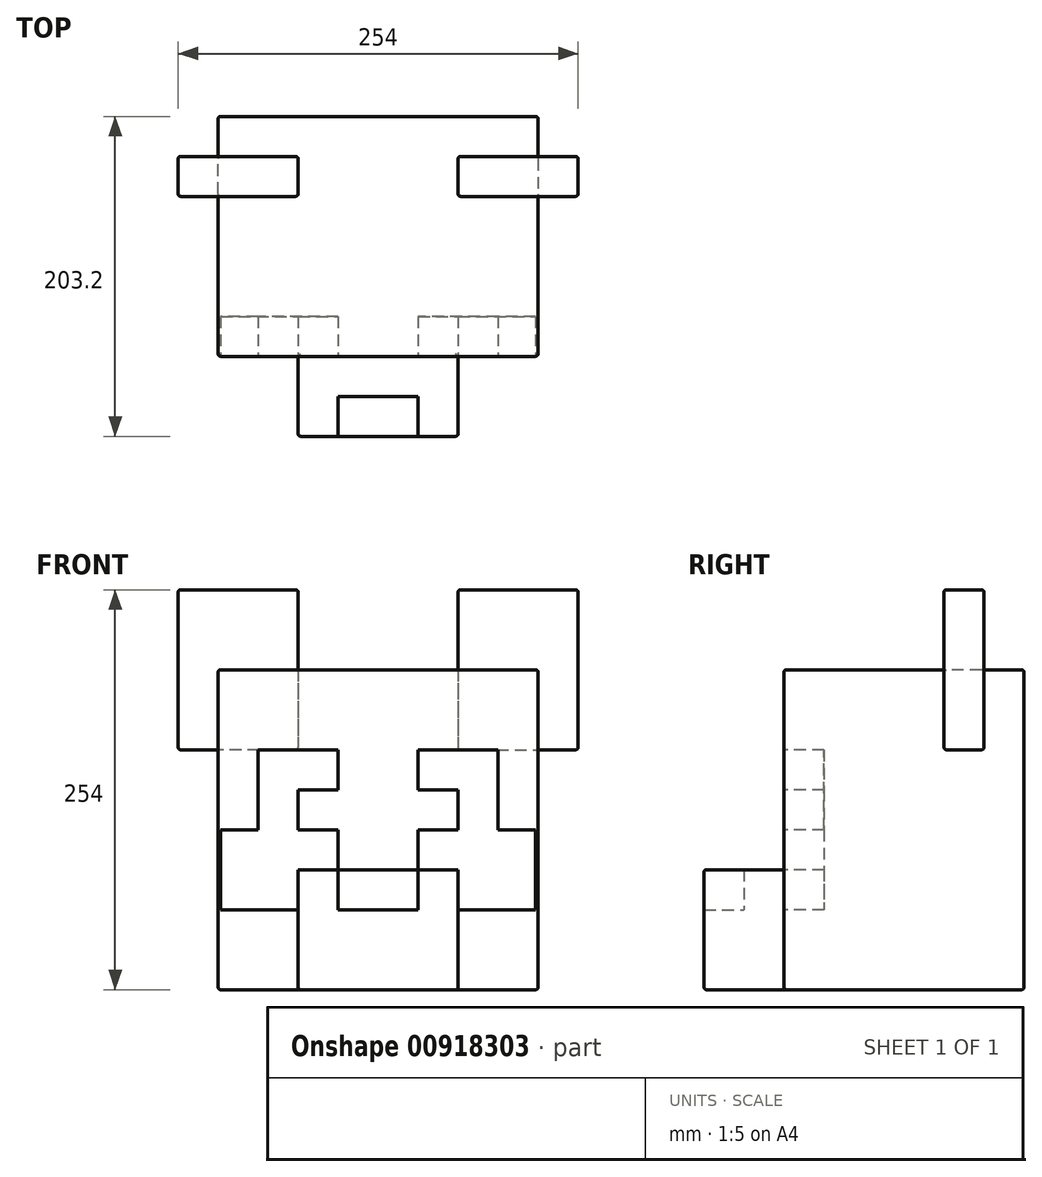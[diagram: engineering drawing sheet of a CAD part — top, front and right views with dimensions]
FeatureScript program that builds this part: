
annotation { "Feature Type Name" : "Feature", "Feature Type Description" : "" }
export const myFeature = defineFeature(function(context is Context, id is Id, definition is map)
    precondition{}
    {
        {
            var Q0;
            Q0=qCreatedBy(makeId("Front.planeOp"),FACE);
            var sketch = newSketch(context, id + "F0", { "sketchPlane" : qUnion([Q0])});
            skLineSegment(sketch, "E0", {"start": v(25.4, 50.8) * mm, "end": v(25.4, 25.4) * mm});
            skLineSegment(sketch, "E1", {"start": v(25.4, 25.4) * mm, "end": v(50.8, 25.4) * mm});
            skLineSegment(sketch, "E2", {"start": v(50.8, 25.4) * mm, "end": v(50.8, 0) * mm});
            skLineSegment(sketch, "E3.bottom", {"start": v(101.6, 101.6) * mm, "end": v(-101.6, 101.6) * mm});
            skLineSegment(sketch, "E3.top", {"start": v(101.6, -101.6) * mm, "end": v(-101.6, -101.6) * mm});
            skLineSegment(sketch, "E3.left", {"start": v(101.6, 101.6) * mm, "end": v(101.6, -101.6) * mm});
            skLineSegment(sketch, "E3.right", {"start": v(-101.6, 101.6) * mm, "end": v(-101.6, -101.6) * mm});
            skPoint(sketch, "E3.middle", {"position": v(0, 0) * mm});
            skPoint(sketch, "E4", {"position": v(101.6, 76.2) * mm});
            skPoint(sketch, "E5", {"position": v(101.6, 50.8) * mm});
            skPoint(sketch, "E6", {"position": v(101.6, 25.4) * mm});
            skPoint(sketch, "E7", {"position": v(101.6, 0) * mm});
            skPoint(sketch, "E8", {"position": v(101.6, -25.4) * mm});
            skPoint(sketch, "E9", {"position": v(101.6, -50.8) * mm});
            skPoint(sketch, "E10", {"position": v(101.6, -76.2) * mm});
            skPoint(sketch, "E11", {"position": v(76.2, 101.6) * mm});
            skPoint(sketch, "E12", {"position": v(50.8, 101.6) * mm});
            skPoint(sketch, "E13", {"position": v(25.4, 101.6) * mm});
            skPoint(sketch, "E14", {"position": v(0, 101.6) * mm});
            skPoint(sketch, "E15", {"position": v(-25.4, 101.6) * mm});
            skPoint(sketch, "E16", {"position": v(-50.8, 101.6) * mm});
            skPoint(sketch, "E17", {"position": v(-76.2, 101.6) * mm});
            skLineSegment(sketch, "E18", {"start": v(25.4, 50.8) * mm, "end": v(76.2, 50.8) * mm});
            skLineSegment(sketch, "E19", {"start": v(50.8, 0) * mm, "end": v(25.4, 0) * mm});
            skLineSegment(sketch, "E20", {"start": v(25.4, 0) * mm, "end": v(25.4, -25.4) * mm});
            skLineSegment(sketch, "E21", {"start": v(25.4, -25.4) * mm, "end": v(50.8, -25.4) * mm});
            skLineSegment(sketch, "E22", {"start": v(50.8, -25.4) * mm, "end": v(50.8, -50.8) * mm});
            skLineSegment(sketch, "E23", {"start": v(50.8, -50.8) * mm, "end": v(101.6, -50.8) * mm});
            skLineSegment(sketch, "E24", {"start": v(76.2, 50.8) * mm, "end": v(76.2, 0) * mm});
            skLineSegment(sketch, "E25", {"start": v(50.8, -50.8) * mm, "end": v(50.8, -101.6) * mm});
            skLineSegment(sketch, "E26", {"start": v(0, 101.6) * mm, "end": v(0, -101.6) * mm, "construction": true});
            skLineSegment(sketch, "E27.MirrorCS", {"start": v(-50.8, -25.4) * mm, "end": v(-50.8, -50.8) * mm});
            skLineSegment(sketch, "E28.MirrorCS", {"start": v(-25.4, 50.8) * mm, "end": v(-76.2, 50.8) * mm});
            skLineSegment(sketch, "E29.MirrorCS", {"start": v(-50.8, -50.8) * mm, "end": v(-101.6, -50.8) * mm});
            skLineSegment(sketch, "E30.MirrorCS", {"start": v(-25.4, 0) * mm, "end": v(-25.4, -25.4) * mm});
            skLineSegment(sketch, "E31.MirrorCS", {"start": v(-76.2, 50.8) * mm, "end": v(-76.2, 0) * mm});
            skLineSegment(sketch, "E32.MirrorCS", {"start": v(-25.4, -25.4) * mm, "end": v(-50.8, -25.4) * mm});
            skLineSegment(sketch, "E33.MirrorCS", {"start": v(-25.4, 25.4) * mm, "end": v(-50.8, 25.4) * mm});
            skLineSegment(sketch, "E34.MirrorCS", {"start": v(-50.8, 0) * mm, "end": v(-25.4, 0) * mm});
            skLineSegment(sketch, "E35.MirrorCS", {"start": v(-50.8, -50.8) * mm, "end": v(-50.8, -101.6) * mm});
            skLineSegment(sketch, "E36.MirrorCS", {"start": v(-25.4, 50.8) * mm, "end": v(-25.4, 25.4) * mm});
            skLineSegment(sketch, "E37.MirrorCS", {"start": v(-50.8, 25.4) * mm, "end": v(-50.8, 0) * mm});
            skLineSegment(sketch, "E38", {"start": v(-25.4, -25.4) * mm, "end": v(25.4, -25.4) * mm});
            skPoint(sketch, "E39.MirrorCS.end.orphan", {"position": v(-101.6, 25.4) * mm});
            skLineSegment(sketch, "E40", {"start": v(76.2, 0) * mm, "end": v(101.6, 0) * mm});
            skLineSegment(sketch, "E41.MirrorCS", {"start": v(-76.2, 0) * mm, "end": v(-101.6, 0) * mm});
            skSolve(sketch);
        }
        {
            var Q0;
            Q0=makeQuery(id+"F0.imprint","IMPRINT",FACE,{"disambiguationData":[TD([[makeQuery(id+"F0.imprint","IMPRINT",EDGE,{"derivedFrom":sQuery(id+"F0.wireOp",EDGE,"E0")}),-1.0]])]});
            var Q1;
            Q1=makeQuery(id+"F0.imprint","IMPRINT",FACE,{"disambiguationData":[TD([[makeQuery(id+"F0.imprint","IMPRINT",EDGE,{"derivedFrom":sQuery(id+"F0.wireOp",EDGE,"E28.MirrorCS")}),1.0]])]});
            var Q2;
            Q2=makeQuery(id+"F0.imprint","IMPRINT",FACE,{"disambiguationData":[TD([[makeQuery(id+"F0.imprint","IMPRINT",EDGE,{"derivedFrom":sQuery(id+"F0.wireOp",EDGE,"E0")}),1.0]])]});
            var Q3;
            Q3=makeQuery(id+"F0.imprint","IMPRINT",FACE,{"disambiguationData":[TD([[makeQuery(id+"F0.imprint","IMPRINT",EDGE,{"derivedFrom":sQuery(id+"F0.wireOp",EDGE,"E27.MirrorCS")}),-1.0]])]});
            var Q4;
            Q4=makeQuery(id+"F0.imprint","IMPRINT",FACE,{"disambiguationData":[TD([[makeQuery(id+"F0.imprint","IMPRINT",EDGE,{"derivedFrom":sQuery(id+"F0.wireOp",EDGE,"E2")}),1.0]])]});
            var Q5;
            {var subQ4=sQuery(id+"F0.wireOp",EDGE,"E29.MirrorCS");Q5=makeQuery(id+"F0.imprint","IMPRINT",FACE,{"disambiguationData":[TD([[makeQuery(id+"F0.imprint","IMPRINT",EDGE,{"derivedFrom":subQ4}),1.0]])]});}
            var Q6;
            Q6=makeQuery(id+"F0.imprint","IMPRINT",FACE,{"disambiguationData":[TD([[makeQuery(id+"F0.imprint","IMPRINT",EDGE,{"derivedFrom":sQuery(id+"F0.wireOp",EDGE,"E21")}),-1.0]])]});
            var Q7;
            {var subQ4=sQuery(id+"F0.wireOp",EDGE,"E23");Q7=makeQuery(id+"F0.imprint","IMPRINT",FACE,{"disambiguationData":[TD([[makeQuery(id+"F0.imprint","IMPRINT",EDGE,{"derivedFrom":subQ4}),-1.0]])]});}
            extrude(context, id + "F1", {"entities" : qUnion([Q0, Q1, Q2, Q3, Q4, Q5, Q6, Q7]), "oppositeDirection" : true, "depth" : 152.4 * mm, "offsetDistance" : 25.4 * mm});
        }
        {
            var Q0;
            Q0=makeQuery(id+"F0.imprint","IMPRINT",FACE,{"disambiguationData":[TD([[makeQuery(id+"F0.imprint","IMPRINT",EDGE,{"derivedFrom":sQuery(id+"F0.wireOp",EDGE,"E21")}),-1.0]])]});
            extrude(context, id + "F2", {"entities" : qUnion([Q0]), "operationType" : NewBodyOperationType.ADD, "depth" : 50.8 * mm, "offsetDistance" : 25.4 * mm});
        }
        {
            var Q0;
            Q0=makeQuery(id+"F2.opExtrude","CAP_FACE",FACE,{"disambiguationData":[OSD([sQuery(id+"F0.wireOp",EDGE,"E3.top"),sQuery(id+"F0.wireOp",EDGE,"E21"),sQuery(id+"F0.wireOp",EDGE,"E22"),sQuery(id+"F0.wireOp",EDGE,"E25"),sQuery(id+"F0.wireOp",EDGE,"E27.MirrorCS"),sQuery(id+"F0.wireOp",EDGE,"E32.MirrorCS"),sQuery(id+"F0.wireOp",EDGE,"E35.MirrorCS"),sQuery(id+"F0.wireOp",EDGE,"E38")])],"isStart":false});
            var sketch = newSketch(context, id + "F3", { "sketchPlane" : qUnion([Q0])});
            skLineSegment(sketch, "E42", {"start": v(-25.4, -25.4) * mm, "end": v(25.4, -25.4) * mm});
            skLineSegment(sketch, "E43", {"start": v(25.4, -25.4) * mm, "end": v(25.4, -50.8) * mm});
            skLineSegment(sketch, "E44", {"start": v(25.4, -50.8) * mm, "end": v(-25.4, -50.8) * mm});
            skLineSegment(sketch, "E45", {"start": v(-25.4, -50.8) * mm, "end": v(-25.4, -25.4) * mm});
            skSolve(sketch);
        }
        {
            var Q0;
            Q0=makeQuery(id+"F3.imprint","IMPRINT",FACE,{"disambiguationData":[TD([[makeQuery(id+"F3.imprint","IMPRINT",EDGE,{"derivedFrom":sQuery(id+"F3.wireOp",EDGE,"E42")}),-1.0]])]});
            extrude(context, id + "F4", {"entities" : qUnion([Q0]), "operationType" : NewBodyOperationType.REMOVE, "oppositeDirection" : true, "depth" : 25.4 * mm, "offsetDistance" : 25.4 * mm});
        }
        {
            var Q0;
            Q0=makeQuery(id+"F4.boolean.opBoolean","COPY",FACE,{"derivedFrom":makeQuery(id+"F4.opExtrude","CAP_FACE",FACE,{"disambiguationData":[OSD([sQuery(id+"F3.wireOp",EDGE,"E42"),sQuery(id+"F3.wireOp",EDGE,"E43"),sQuery(id+"F3.wireOp",EDGE,"E44"),sQuery(id+"F3.wireOp",EDGE,"E45")])],"isStart":false})});
            extrude(context, id + "F5", {"entities" : qUnion([Q0]), "depth" : 25.4 * mm, "offsetDistance" : 25.4 * mm});
        }
        {
            var Q0;
            Q0=qCreatedBy(makeId("Front.planeOp"),FACE);
            cPlane(context, id + "F6", {"entities" : qUnion([Q0]), "cplaneType" : CPlaneType.OFFSET, "offset" : 101.6 * mm, "oppositeDirection" : true, "width" : 152.4 * mm, "height" : 152.4 * mm});
        }
        {
            var Q0;
            Q0=qCreatedBy(id+"F6.planeOp",FACE);
            var sketch = newSketch(context, id + "F7", { "sketchPlane" : qUnion([Q0])});
            skLineSegment(sketch, "E46", {"start": v(50.8, 101.6) * mm, "end": v(50.8, 152.4) * mm});
            skLineSegment(sketch, "E47", {"start": v(50.8, 152.4) * mm, "end": v(127, 152.4) * mm});
            skLineSegment(sketch, "E48", {"start": v(127, 152.4) * mm, "end": v(127, 50.8) * mm});
            skLineSegment(sketch, "E49", {"start": v(127, 50.8) * mm, "end": v(101.6, 50.8) * mm});
            skLineSegment(sketch, "E50", {"start": v(101.6, 50.8) * mm, "end": v(101.6, 101.6) * mm});
            skLineSegment(sketch, "E51", {"start": v(101.6, 101.6) * mm, "end": v(50.8, 101.6) * mm});
            skLineSegment(sketch, "E52", {"start": v(50.8, 101.6) * mm, "end": v(50.8, 50.8) * mm});
            skLineSegment(sketch, "E53", {"start": v(50.8, 50.8) * mm, "end": v(101.6, 50.8) * mm});
            skLineSegment(sketch, "E54.MirrorCS", {"start": v(-50.8, 50.8) * mm, "end": v(-101.6, 50.8) * mm});
            skLineSegment(sketch, "E55.MirrorCS", {"start": v(-50.8, 101.6) * mm, "end": v(-50.8, 50.8) * mm});
            skLineSegment(sketch, "E56.MirrorCS", {"start": v(-50.8, 101.6) * mm, "end": v(-50.8, 152.4) * mm});
            skLineSegment(sketch, "E57.MirrorCS", {"start": v(-50.8, 152.4) * mm, "end": v(-127, 152.4) * mm});
            skLineSegment(sketch, "E58.MirrorCS", {"start": v(-127, 152.4) * mm, "end": v(-127, 50.8) * mm});
            skLineSegment(sketch, "E59.MirrorCS", {"start": v(-127, 50.8) * mm, "end": v(-101.6, 50.8) * mm});
            skSolve(sketch);
        }
        {
            var Q0;
            Q0=makeQuery(id+"F7.imprint","IMPRINT",FACE,{"disambiguationData":[TD([[makeQuery(id+"F7.imprint","IMPRINT",EDGE,{"derivedFrom":sQuery(id+"F7.wireOp",EDGE,"E50")}),1.0]])]});
            var Q1;
            Q1=makeQuery(id+"F7.imprint","IMPRINT",FACE,{"disambiguationData":[TD([[makeQuery(id+"F7.imprint","IMPRINT",EDGE,{"derivedFrom":sQuery(id+"F7.wireOp",EDGE,"E46")}),-1.0]])]});
            var Q2;
            Q2=makeQuery(id+"F7.imprint","IMPRINT",FACE,{"disambiguationData":[TD([[makeQuery(id+"F7.imprint","IMPRINT",EDGE,{"derivedFrom":sQuery(id+"F7.wireOp",EDGE,"E54.MirrorCS")}),-1.0]])]});
            extrude(context, id + "F8", {"entities" : qUnion([Q0, Q1, Q2]), "oppositeDirection" : true, "depth" : 25.4 * mm, "offsetDistance" : 25.4 * mm});
        }
        {
            var Q0;
            {var subQ0=sQuery(id+"F0.wireOp",EDGE,"E38");var subQ2=sQuery(id+"F0.wireOp",EDGE,"E32.MirrorCS");var subQ4=sQuery(id+"F0.wireOp",EDGE,"E21");Q0=makeQuery(id+"F4.boolean.opBoolean","SPLIT",EDGE,{"disambiguationData":[TD([makeQuery(id+"F4.opExtrude","SWEPT_FACE",FACE,{"disambiguationData":[OSD([sQuery(id+"F3.wireOp",EDGE,"E45")])]})])],"derivedFrom":makeQuery(id+"F2.opExtrude","CAP_EDGE",EDGE,{"disambiguationData":[OSD([subQ4,subQ2,subQ0])],"isStart":false})});}
            var Q1;
            Q1=makeQuery(id+"F5.opExtrude","CAP_EDGE",EDGE,{"disambiguationData":[OSD([sQuery(id+"F3.wireOp",EDGE,"E42")])],"isStart":false});
            var Q2;
            {var subQ0=sQuery(id+"F0.wireOp",EDGE,"E38");var subQ1=sQuery(id+"F0.wireOp",EDGE,"E32.MirrorCS");var subQ4=sQuery(id+"F0.wireOp",EDGE,"E21");Q2=makeQuery(id+"F4.boolean.opBoolean","SPLIT",EDGE,{"disambiguationData":[TD([makeQuery(id+"F4.opExtrude","SWEPT_FACE",FACE,{"disambiguationData":[OSD([sQuery(id+"F3.wireOp",EDGE,"E43")])]})])],"derivedFrom":makeQuery(id+"F2.opExtrude","CAP_EDGE",EDGE,{"disambiguationData":[OSD([subQ4,subQ1,subQ0])],"isStart":false})});}
            var Q3;
            {var subQ0=sQuery(id+"F0.wireOp",EDGE,"E3.top");Q3=makeQuery(id+"F2.boolean.opBoolean","MERGE",FACE,{"derivedFrom":[makeQuery(id+"F1.opExtrude","SWEPT_FACE",FACE,{"disambiguationData":[OSD([subQ0])]}),makeQuery(id+"F2.opExtrude","SWEPT_FACE",FACE,{"disambiguationData":[OSD([subQ0])]})]});}
            var Q4;
            Q4=makeQuery(id+"F1.opExtrude","CAP_FACE",FACE,{"disambiguationData":[OSD([sQuery(id+"F0.wireOp",EDGE,"E3.bottom"),sQuery(id+"F0.wireOp",EDGE,"E3.top"),sQuery(id+"F0.wireOp",EDGE,"E3.left"),sQuery(id+"F0.wireOp",EDGE,"E3.right")])],"isStart":false});
            var Q5;
            {var subQ0=sQuery(id+"F0.wireOp",EDGE,"E3.bottom");var subQ1=sQuery(id+"F0.wireOp",EDGE,"E3.right");Q5=makeQuery(id+"F5OZuFi827c7V8s_2.boolean.opBoolean","SPLIT",EDGE,{"disambiguationData":[TD([makeQuery(id+"F1.opExtrude","CAP_FACE",FACE,{"disambiguationData":[OSD([subQ0,sQuery(id+"F0.wireOp",EDGE,"E3.top"),sQuery(id+"F0.wireOp",EDGE,"E3.left"),subQ1])],"isStart":false})])],"derivedFrom":makeQuery(id+"F1.opExtrude","SWEPT_EDGE",EDGE,{"disambiguationData":[OSD([subQ0,subQ1])]})});}
            var Q6;
            {var subQ0=sQuery(id+"F0.wireOp",EDGE,"E3.bottom");var subQ1=sQuery(id+"F0.wireOp",EDGE,"E3.right");Q6=makeQuery(id+"F5OZuFi827c7V8s_2.boolean.opBoolean","SPLIT",EDGE,{"disambiguationData":[TD([makeQuery(id+"F1.opExtrude","CAP_FACE",FACE,{"disambiguationData":[OSD([subQ0,sQuery(id+"F0.wireOp",EDGE,"E3.top"),sQuery(id+"F0.wireOp",EDGE,"E3.left"),subQ1])],"isStart":true})])],"derivedFrom":makeQuery(id+"F1.opExtrude","SWEPT_EDGE",EDGE,{"disambiguationData":[OSD([subQ0,subQ1])]})});}
            var Q7;
            {var subQ0=sQuery(id+"F0.wireOp",EDGE,"E3.bottom");var subQ1=sQuery(id+"F0.wireOp",EDGE,"E3.left");Q7=makeQuery(id+"F5OZuFi827c7V8s_2.boolean.opBoolean","SPLIT",EDGE,{"disambiguationData":[TD([makeQuery(id+"F1.opExtrude","CAP_FACE",FACE,{"disambiguationData":[OSD([subQ0,sQuery(id+"F0.wireOp",EDGE,"E3.top"),subQ1,sQuery(id+"F0.wireOp",EDGE,"E3.right")])],"isStart":false})])],"derivedFrom":makeQuery(id+"F1.opExtrude","SWEPT_EDGE",EDGE,{"disambiguationData":[OSD([subQ0,subQ1])]})});}
            var Q8;
            {var subQ0=sQuery(id+"F0.wireOp",EDGE,"E3.bottom");var subQ1=sQuery(id+"F0.wireOp",EDGE,"E3.left");Q8=makeQuery(id+"F5OZuFi827c7V8s_2.boolean.opBoolean","SPLIT",EDGE,{"disambiguationData":[TD([makeQuery(id+"F1.opExtrude","CAP_FACE",FACE,{"disambiguationData":[OSD([subQ0,sQuery(id+"F0.wireOp",EDGE,"E3.top"),subQ1,sQuery(id+"F0.wireOp",EDGE,"E3.right")])],"isStart":true})])],"derivedFrom":makeQuery(id+"F1.opExtrude","SWEPT_EDGE",EDGE,{"disambiguationData":[OSD([subQ0,subQ1])]})});}
            var Q9;
            Q9=makeQuery(id+"F8.opExtrude","CAP_FACE",FACE,{"disambiguationData":[OSD([sQuery(id+"F7.wireOp",EDGE,"E46"),sQuery(id+"F7.wireOp",EDGE,"E47"),sQuery(id+"F7.wireOp",EDGE,"E48"),sQuery(id+"F7.wireOp",EDGE,"E49"),sQuery(id+"F7.wireOp",EDGE,"E52"),sQuery(id+"F7.wireOp",EDGE,"E53")])],"isStart":true});
            var Q10;
            Q10=makeQuery(id+"F8.opExtrude","CAP_FACE",FACE,{"disambiguationData":[OSD([sQuery(id+"F7.wireOp",EDGE,"E46"),sQuery(id+"F7.wireOp",EDGE,"E47"),sQuery(id+"F7.wireOp",EDGE,"E48"),sQuery(id+"F7.wireOp",EDGE,"E49"),sQuery(id+"F7.wireOp",EDGE,"E52"),sQuery(id+"F7.wireOp",EDGE,"E53")])],"isStart":false});
            var Q11;
            Q11=makeQuery(id+"F8.opExtrude","SWEPT_FACE",FACE,{"disambiguationData":[OSD([sQuery(id+"F7.wireOp",EDGE,"E49"),sQuery(id+"F7.wireOp",EDGE,"E53")])]});
            var Q12;
            Q12=makeQuery(id+"F8.opExtrude","SWEPT_FACE",FACE,{"disambiguationData":[OSD([sQuery(id+"F7.wireOp",EDGE,"E47")])]});
            var Q13;
            Q13=makeQuery(id+"F8.opExtrude","CAP_FACE",FACE,{"disambiguationData":[OSD([sQuery(id+"F7.wireOp",EDGE,"E54.MirrorCS"),sQuery(id+"F7.wireOp",EDGE,"E55.MirrorCS"),sQuery(id+"F7.wireOp",EDGE,"E56.MirrorCS"),sQuery(id+"F7.wireOp",EDGE,"E57.MirrorCS"),sQuery(id+"F7.wireOp",EDGE,"E58.MirrorCS"),sQuery(id+"F7.wireOp",EDGE,"E59.MirrorCS")])],"isStart":false});
            var Q14;
            Q14=makeQuery(id+"F8.opExtrude","CAP_FACE",FACE,{"disambiguationData":[OSD([sQuery(id+"F7.wireOp",EDGE,"E54.MirrorCS"),sQuery(id+"F7.wireOp",EDGE,"E55.MirrorCS"),sQuery(id+"F7.wireOp",EDGE,"E56.MirrorCS"),sQuery(id+"F7.wireOp",EDGE,"E57.MirrorCS"),sQuery(id+"F7.wireOp",EDGE,"E58.MirrorCS"),sQuery(id+"F7.wireOp",EDGE,"E59.MirrorCS")])],"isStart":true});
            var Q15;
            Q15=makeQuery(id+"F8.opExtrude","SWEPT_FACE",FACE,{"disambiguationData":[OSD([sQuery(id+"F7.wireOp",EDGE,"E54.MirrorCS"),sQuery(id+"F7.wireOp",EDGE,"E59.MirrorCS")])]});
            var Q16;
            Q16=makeQuery(id+"F8.opExtrude","SWEPT_FACE",FACE,{"disambiguationData":[OSD([sQuery(id+"F7.wireOp",EDGE,"E57.MirrorCS")])]});
            var Q17;
            Q17=makeQuery(id+"F2.opExtrude","CAP_EDGE",EDGE,{"disambiguationData":[OSD([sQuery(id+"F0.wireOp",EDGE,"E22"),sQuery(id+"F0.wireOp",EDGE,"E25")])],"isStart":false});
            var Q18;
            Q18=makeQuery(id+"F2.opExtrude","SWEPT_EDGE",EDGE,{"disambiguationData":[OSD([sQuery(id+"F0.wireOp",EDGE,"E21"),sQuery(id+"F0.wireOp",EDGE,"E22")])]});
            var Q19;
            Q19=makeQuery(id+"F2.opExtrude","CAP_EDGE",EDGE,{"disambiguationData":[OSD([sQuery(id+"F0.wireOp",EDGE,"E27.MirrorCS"),sQuery(id+"F0.wireOp",EDGE,"E35.MirrorCS")])],"isStart":false});
            var Q20;
            Q20=makeQuery(id+"F2.opExtrude","SWEPT_EDGE",EDGE,{"disambiguationData":[OSD([sQuery(id+"F0.wireOp",EDGE,"E27.MirrorCS"),sQuery(id+"F0.wireOp",EDGE,"E32.MirrorCS")])]});
            var Q21;
            Q21=makeQuery(id+"F1.opExtrude","CAP_EDGE",EDGE,{"disambiguationData":[OSD([sQuery(id+"F0.wireOp",EDGE,"E3.left")])],"isStart":true});
            var Q22;
            Q22=makeQuery(id+"F1.opExtrude","CAP_EDGE",EDGE,{"disambiguationData":[OSD([sQuery(id+"F0.wireOp",EDGE,"E3.bottom")])],"isStart":true});
            var Q23;
            Q23=makeQuery(id+"F1.opExtrude","CAP_EDGE",EDGE,{"disambiguationData":[OSD([sQuery(id+"F0.wireOp",EDGE,"E3.right")])],"isStart":true});
            fillet(context, id + "F9", {"entities" : qUnion([Q0, Q1, Q2, Q3, Q4, Q5, Q6, Q7, Q8, Q9, Q10, Q11, Q12, Q13, Q14, Q15, Q16, Q17, Q18, Q19, Q20, Q21, Q22, Q23]), "radius" : 1.52 * mm, "tangentPropagation" : true, "allowEdgeOverflow" : false});
        }
        {
            var Q0;
            Q0=makeQuery(id+"F8.opExtrude","SWEPT_BODY",BODY,{"disambiguationData":[OSD([sQuery(id+"F7.wireOp",EDGE,"E46"),sQuery(id+"F7.wireOp",EDGE,"E47"),sQuery(id+"F7.wireOp",EDGE,"E48"),sQuery(id+"F7.wireOp",EDGE,"E49"),sQuery(id+"F7.wireOp",EDGE,"E52"),sQuery(id+"F7.wireOp",EDGE,"E53")])]});
            var Q1;
            Q1=makeQuery(id+"F8.opExtrude","SWEPT_BODY",BODY,{"disambiguationData":[OSD([sQuery(id+"F7.wireOp",EDGE,"E54.MirrorCS"),sQuery(id+"F7.wireOp",EDGE,"E55.MirrorCS"),sQuery(id+"F7.wireOp",EDGE,"E56.MirrorCS"),sQuery(id+"F7.wireOp",EDGE,"E57.MirrorCS"),sQuery(id+"F7.wireOp",EDGE,"E58.MirrorCS"),sQuery(id+"F7.wireOp",EDGE,"E59.MirrorCS")])]});
            var Q2;
            Q2=makeQuery(id+"F1.opExtrude","SWEPT_BODY",BODY,{"disambiguationData":[OSD([sQuery(id+"F0.wireOp",EDGE,"E3.bottom"),sQuery(id+"F0.wireOp",EDGE,"E3.top"),sQuery(id+"F0.wireOp",EDGE,"E3.left"),sQuery(id+"F0.wireOp",EDGE,"E3.right")])]});
            booleanBodies(context, id + "F10", {"operationType" : BooleanOperationType.SUBTRACTION, "tools" : qUnion([Q0, Q1]), "targets" : qUnion([Q2]), "keepTools" : true});
        }
        {
            var Q0;
            Q0=qCreatedBy(makeId("Front.planeOp"),FACE);
            var sketch = newSketch(context, id + "F11", { "sketchPlane" : qUnion([Q0])});
            skLineSegment(sketch, "E60.0.0", {"start": v(-76.2, 0) * mm, "end": v(-100.08, 0) * mm});
            skLineSegment(sketch, "E60.0.2", {"start": v(-100.08, -50.8) * mm, "end": v(-50.8, -50.8) * mm});
            skLineSegment(sketch, "E60.0.3", {"start": v(-50.8, -50.8) * mm, "end": v(-50.8, -25.4) * mm});
            skLineSegment(sketch, "E60.0.4", {"start": v(-50.8, -25.4) * mm, "end": v(-25.4, -25.4) * mm});
            skLineSegment(sketch, "E60.0.5", {"start": v(-25.4, -25.4) * mm, "end": v(-25.4, 0) * mm});
            skLineSegment(sketch, "E60.0.6", {"start": v(-25.4, 0) * mm, "end": v(-50.8, 0) * mm});
            skLineSegment(sketch, "E60.0.7", {"start": v(-50.8, 0) * mm, "end": v(-50.8, 25.4) * mm});
            skLineSegment(sketch, "E60.0.8", {"start": v(-50.8, 25.4) * mm, "end": v(-25.4, 25.4) * mm});
            skLineSegment(sketch, "E60.0.9", {"start": v(-25.4, 25.4) * mm, "end": v(-25.4, 50.8) * mm});
            skLineSegment(sketch, "E60.0.10", {"start": v(-25.4, 50.8) * mm, "end": v(-76.2, 50.8) * mm});
            skLineSegment(sketch, "E60.0.11", {"start": v(-76.2, 50.8) * mm, "end": v(-76.2, 0) * mm});
            skLineSegment(sketch, "E61.0.1", {"start": v(100.08, 0) * mm, "end": v(76.2, 0) * mm});
            skLineSegment(sketch, "E61.0.2", {"start": v(76.2, 0) * mm, "end": v(76.2, 50.8) * mm});
            skLineSegment(sketch, "E61.0.3", {"start": v(76.2, 50.8) * mm, "end": v(25.4, 50.8) * mm});
            skLineSegment(sketch, "E61.0.4", {"start": v(25.4, 50.8) * mm, "end": v(25.4, 25.4) * mm});
            skLineSegment(sketch, "E61.0.5", {"start": v(25.4, 25.4) * mm, "end": v(50.8, 25.4) * mm});
            skLineSegment(sketch, "E61.0.6", {"start": v(50.8, 25.4) * mm, "end": v(50.8, 0) * mm});
            skLineSegment(sketch, "E61.0.7", {"start": v(50.8, 0) * mm, "end": v(25.4, 0) * mm});
            skLineSegment(sketch, "E61.0.8", {"start": v(25.4, 0) * mm, "end": v(25.4, -25.4) * mm});
            skLineSegment(sketch, "E61.0.9", {"start": v(25.4, -25.4) * mm, "end": v(50.8, -25.4) * mm});
            skLineSegment(sketch, "E61.0.10", {"start": v(50.8, -25.4) * mm, "end": v(50.8, -50.8) * mm});
            skLineSegment(sketch, "E61.0.11", {"start": v(50.8, -50.8) * mm, "end": v(100.08, -50.8) * mm});
            skLineSegment(sketch, "E62", {"start": v(100.08, 0) * mm, "end": v(100.08, -50.8) * mm});
            skPoint(sketch, "E63.orphan", {"position": v(101.6, 0) * mm});
            skPoint(sketch, "E64.orphan", {"position": v(101.6, -50.8) * mm});
            skLineSegment(sketch, "E65", {"start": v(-100.08, 0) * mm, "end": v(-100.08, -50.8) * mm});
            skPoint(sketch, "E66.orphan", {"position": v(-101.6, 0) * mm});
            skPoint(sketch, "E67.orphan", {"position": v(-101.6, -50.8) * mm});
            skSolve(sketch);
        }
        {
            var Q0;
            Q0=makeQuery(id+"F11.imprint","IMPRINT",FACE,{"disambiguationData":[TD([[makeQuery(id+"F11.imprint","IMPRINT",EDGE,{"derivedFrom":sQuery(id+"F11.wireOp",EDGE,"E60.0.0")}),1.0]])]});
            var Q1;
            Q1=makeQuery(id+"F11.imprint","IMPRINT",FACE,{"disambiguationData":[TD([[makeQuery(id+"F11.imprint","IMPRINT",EDGE,{"derivedFrom":sQuery(id+"F11.wireOp",EDGE,"E61.0.1")}),1.0]])]});
            extrude(context, id + "F12", {"entities" : qUnion([Q0, Q1]), "operationType" : NewBodyOperationType.REMOVE, "oppositeDirection" : true, "depth" : 25.4 * mm, "offsetDistance" : 25.4 * mm});
        }
        {
            var Q0;
            Q0=makeQuery(id+"F11.imprint","IMPRINT",FACE,{"disambiguationData":[TD([[makeQuery(id+"F11.imprint","IMPRINT",EDGE,{"derivedFrom":sQuery(id+"F11.wireOp",EDGE,"E60.0.0")}),1.0]])]});
            var Q1;
            Q1=makeQuery(id+"F11.imprint","IMPRINT",FACE,{"disambiguationData":[TD([[makeQuery(id+"F11.imprint","IMPRINT",EDGE,{"derivedFrom":sQuery(id+"F11.wireOp",EDGE,"E61.0.1")}),1.0]])]});
            extrude(context, id + "F13", {"entities" : qUnion([Q0, Q1]), "oppositeDirection" : true, "depth" : 25.4 * mm, "offsetDistance" : 25.4 * mm});
        }
    });
